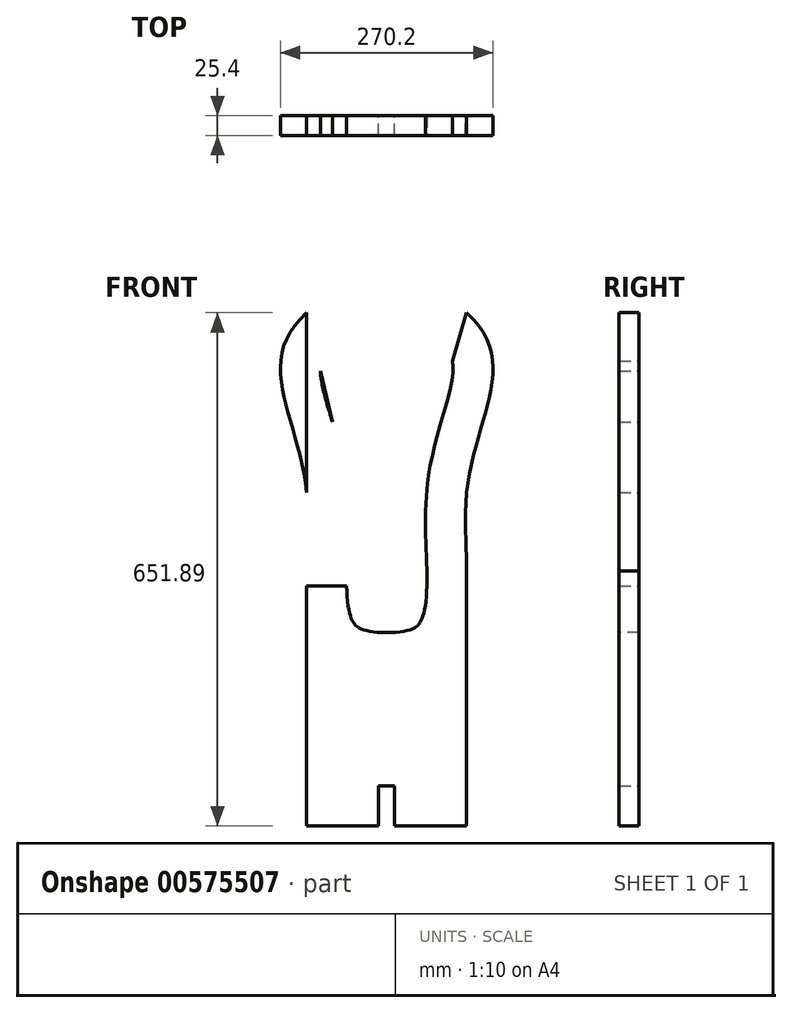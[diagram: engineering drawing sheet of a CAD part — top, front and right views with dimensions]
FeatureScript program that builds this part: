
annotation { "Feature Type Name" : "Feature", "Feature Type Description" : "" }
export const myFeature = defineFeature(function(context is Context, id is Id, definition is map)
    precondition{}
    {
        {
            var Q0;
            Q0=qCreatedBy(makeId("Front.planeOp"),FACE);
            var sketch = newSketch(context, id + "F0", { "sketchPlane" : qUnion([Q0])});
            skLineSegment(sketch, "E0", {"start": v(-101.6, 177.6) * mm, "end": v(-101.6, -279.6) * mm});
            skLineSegment(sketch, "E1.MirrorCS", {"start": v(101.6, 177.6) * mm, "end": v(101.6, -279.6) * mm});
            skLineSegment(sketch, "E2", {"start": v(-101.6, -279.6) * mm, "end": v(101.6, -279.6) * mm});
            skFitSpline(sketch, "E3", {"points": [v(0, -279.6) * mm, v(101.6, -51) * mm, v(101.6, 177.6) * mm], "startDerivative": vector(812.4, 0) * mm, "endDerivative": vector(-432.42, 390.54) * mm});
            skFitSpline(sketch, "E4.MirrorCS", {"points": [v(0, -279.6) * mm, v(-101.6, -51) * mm, v(-101.6, 177.6) * mm], "startDerivative": vector(-812.4, 0) * mm, "endDerivative": vector(432.42, 390.54) * mm});
            skFitSpline(sketch, "E5.0", {"points": [v(0, -228.8) * mm, v(-3.27, -228.8) * mm, v(-9.34, -228.62) * mm, v(-17.06, -227.88) * mm, v(-23.42, -226.8) * mm, v(-28.5, -225.5) * mm, v(-32.37, -224.1) * mm, v(-35.24, -222.75) * mm, v(-37.31, -221.48) * mm, v(-38.86, -220.29) * mm, v(-40.12, -219.07) * mm, v(-41.3, -217.68) * mm, v(-42.5, -215.9) * mm, v(-43.75, -213.58) * mm, v(-45.04, -210.6) * mm, v(-46.3, -206.88) * mm, v(-47.48, -202.42) * mm, v(-48.87, -195.5) * mm, v(-50.16, -185.15) * mm, v(-50.9, -170.43) * mm, v(-50.92, -153.85) * mm, v(-50.46, -135.8) * mm, v(-49.8, -116.57) * mm, v(-49.36, -99.78) * mm, v(-49.25, -85.97) * mm, v(-49.34, -77.2) * mm, v(-49.52, -70.1) * mm, v(-49.72, -64.75) * mm, v(-50, -59.36) * mm, v(-50.35, -53.93) * mm, v(-50.72, -49.38) * mm, v(-51.07, -45.72) * mm, v(-51.45, -42.07) * mm, v(-51.98, -37.56) * mm, v(-52.93, -30.46) * mm, v(-54.31, -21.78) * mm, v(-56.22, -11.7) * mm, v(-58.32, -1.93) * mm, v(-60.56, 7.5) * mm, v(-62.9, 16.61) * mm, v(-66.1, 28.32) * mm, v(-70.11, 42.15) * mm, v(-74.61, 57.4) * mm, v(-78.5, 71.28) * mm, v(-81.52, 83.68) * mm, v(-83.16, 92.65) * mm, v(-83.94, 98.95) * mm, v(-84.26, 103.23) * mm, v(-84.34, 107.06) * mm, v(-84.2, 110.48) * mm, v(-83.87, 113.52) * mm, v(-83.36, 116.26) * mm, v(-82.69, 118.8) * mm, v(-81.82, 121.26) * mm, v(-80.7, 123.76) * mm, v(-79.23, 126.41) * mm, v(-77.32, 129.3) * mm, v(-74.84, 132.5) * mm, v(-71.67, 136) * mm, v(-69.02, 138.56) * mm, v(-67.55, 139.9) * mm]});
            skFitSpline(sketch, "E5.1", {"points": [v(0, -228.8) * mm, v(3.27, -228.8) * mm, v(9.34, -228.62) * mm, v(17.06, -227.88) * mm, v(23.42, -226.8) * mm, v(28.5, -225.5) * mm, v(32.37, -224.1) * mm, v(35.24, -222.75) * mm, v(37.31, -221.48) * mm, v(38.86, -220.29) * mm, v(40.12, -219.07) * mm, v(41.3, -217.68) * mm, v(42.5, -215.9) * mm, v(43.75, -213.58) * mm, v(45.04, -210.6) * mm, v(46.3, -206.88) * mm, v(47.48, -202.42) * mm, v(48.87, -195.5) * mm, v(50.16, -185.15) * mm, v(50.9, -170.43) * mm, v(50.92, -153.85) * mm, v(50.46, -135.8) * mm, v(49.8, -116.57) * mm, v(49.36, -99.78) * mm, v(49.25, -85.97) * mm, v(49.34, -77.2) * mm, v(49.52, -70.1) * mm, v(49.72, -64.75) * mm, v(50, -59.36) * mm, v(50.35, -53.93) * mm, v(50.72, -49.38) * mm, v(51.07, -45.72) * mm, v(51.45, -42.07) * mm, v(51.98, -37.56) * mm, v(52.93, -30.46) * mm, v(54.31, -21.78) * mm, v(56.22, -11.7) * mm, v(58.32, -1.93) * mm, v(60.56, 7.5) * mm, v(62.9, 16.61) * mm, v(66.1, 28.32) * mm, v(70.11, 42.15) * mm, v(74.61, 57.4) * mm, v(78.5, 71.28) * mm, v(81.52, 83.68) * mm, v(83.16, 92.65) * mm, v(83.94, 98.95) * mm, v(84.26, 103.23) * mm, v(84.34, 107.06) * mm, v(84.2, 110.48) * mm, v(83.87, 113.52) * mm, v(83.36, 116.26) * mm, v(82.69, 118.8) * mm, v(81.82, 121.26) * mm, v(80.7, 123.76) * mm, v(79.23, 126.41) * mm, v(77.32, 129.3) * mm, v(74.84, 132.5) * mm, v(71.67, 136) * mm, v(69.02, 138.56) * mm, v(67.55, 139.9) * mm]});
            skLineSegment(sketch, "E6", {"start": v(-101.6, 177.6) * mm, "end": v(-68.99, 38.25) * mm});
            skLineSegment(sketch, "E7", {"start": v(101.6, 177.6) * mm, "end": v(83.41, 115.87) * mm});
            skLineSegment(sketch, "E8", {"start": v(-101.6, -169.5) * mm, "end": v(101.6, -169.5) * mm});
            skLineSegment(sketch, "E9", {"start": v(-101.6, -169.5) * mm, "end": v(-101.6, -474.3) * mm});
            skLineSegment(sketch, "E10", {"start": v(-101.6, -474.3) * mm, "end": v(101.6, -474.3) * mm});
            skLineSegment(sketch, "E11", {"start": v(101.6, -474.3) * mm, "end": v(101.6, -169.5) * mm});
            skLineSegment(sketch, "E12.bottom", {"start": v(10.16, -525.1) * mm, "end": v(-10.16, -525.1) * mm});
            skLineSegment(sketch, "E12.top", {"start": v(10.16, -423.5) * mm, "end": v(-10.16, -423.5) * mm});
            skLineSegment(sketch, "E12.left", {"start": v(10.16, -525.1) * mm, "end": v(10.16, -423.5) * mm});
            skLineSegment(sketch, "E12.right", {"start": v(-10.16, -525.1) * mm, "end": v(-10.16, -423.5) * mm});
            skPoint(sketch, "E12.middle", {"position": v(0, -474.3) * mm});
            skSolve(sketch);
        }
        {
            var Q0;
            {var subQ0=sQuery(id+"F0.wireOp",EDGE,"E7");Q0=makeQuery(id+"F0.imprint","IMPRINT",FACE,{"disambiguationData":[TD([[makeQuery(id+"F0.imprint","IMPRINT",EDGE,{"derivedFrom":subQ0}),1.0]])]});}
            var Q1;
            {var subQ6=sQuery(id+"F0.wireOp",EDGE,"E12.top");Q1=makeQuery(id+"F0.imprint","IMPRINT",FACE,{"disambiguationData":[TD([[makeQuery(id+"F0.imprint","IMPRINT",EDGE,{"derivedFrom":subQ6}),-1.0]])]});}
            var Q2;
            {var subQ1=sQuery(id+"F0.wireOp",EDGE,"E2");var subQ3=sQuery(id+"F0.wireOp",EDGE,"E9");var subQ4=makeQuery(id+"F0.imprint","INTERSECT",VERTEX,{"derivedFrom":[subQ1,subQ3]});Q2=makeQuery(id+"F0.imprint","IMPRINT",FACE,{"disambiguationData":[TD([[makeQuery(id+"F0.imprint","IMPRINT",EDGE,{"disambiguationData":[TD([[subQ4,-1.0]])],"derivedFrom":subQ1}),1.0]])]});}
            var Q3;
            {var subQ1=sQuery(id+"F0.wireOp",EDGE,"E2");var subQ3=sQuery(id+"F0.wireOp",EDGE,"E11");var subQ4=makeQuery(id+"F0.imprint","INTERSECT",VERTEX,{"derivedFrom":[subQ1,subQ3]});Q3=makeQuery(id+"F0.imprint","IMPRINT",FACE,{"disambiguationData":[TD([[makeQuery(id+"F0.imprint","IMPRINT",EDGE,{"disambiguationData":[TD([[subQ4,1.0]])],"derivedFrom":subQ1}),1.0]])]});}
            var Q4;
            {var subQ0=sQuery(id+"F0.wireOp",EDGE,"E5.1");var subQ1=sQuery(id+"F0.wireOp",EDGE,"E5.0");var subQ2=makeQuery(id+"F0.imprint","INTERSECT",VERTEX,{"derivedFrom":[subQ1,subQ0]});Q4=makeQuery(id+"F0.imprint","IMPRINT",FACE,{"disambiguationData":[TD([[makeQuery(id+"F0.imprint","IMPRINT",EDGE,{"disambiguationData":[TD([[subQ2,-1.0]])],"derivedFrom":subQ1}),1.0]])]});}
            var Q5;
            {var subQ0=sQuery(id+"F0.wireOp",EDGE,"E6");Q5=makeQuery(id+"F0.imprint","IMPRINT",FACE,{"disambiguationData":[TD([[makeQuery(id+"F0.imprint","IMPRINT",EDGE,{"derivedFrom":subQ0}),-1.0]])]});}
            var Q6;
            {var subQ0=sQuery(id+"F0.wireOp",EDGE,"E3");var subQ1=sQuery(id+"F0.wireOp",EDGE,"E1.MirrorCS");var subQ3=makeQuery(id+"F0.imprint","INTERSECT",VERTEX,{"derivedFrom":[subQ1,subQ0]});Q6=makeQuery(id+"F0.imprint","IMPRINT",FACE,{"disambiguationData":[TD([[makeQuery(id+"F0.imprint","IMPRINT",EDGE,{"disambiguationData":[TD([[subQ3,1.0]])],"derivedFrom":subQ1}),1.0]])]});}
            var Q7;
            {var subQ0=sQuery(id+"F0.wireOp",EDGE,"E4.MirrorCS");var subQ1=sQuery(id+"F0.wireOp",EDGE,"E0");var subQ3=makeQuery(id+"F0.imprint","INTERSECT",VERTEX,{"derivedFrom":[subQ1,subQ0]});Q7=makeQuery(id+"F0.imprint","IMPRINT",FACE,{"disambiguationData":[TD([[makeQuery(id+"F0.imprint","IMPRINT",EDGE,{"disambiguationData":[TD([[subQ3,1.0]])],"derivedFrom":subQ1}),-1.0]])]});}
            extrude(context, id + "F1", {"entities" : qUnion([Q0, Q1, Q2, Q3, Q4, Q5, Q6, Q7]), "depth" : 25.4 * mm, "offsetDistance" : 25.4 * mm});
        }
    });
